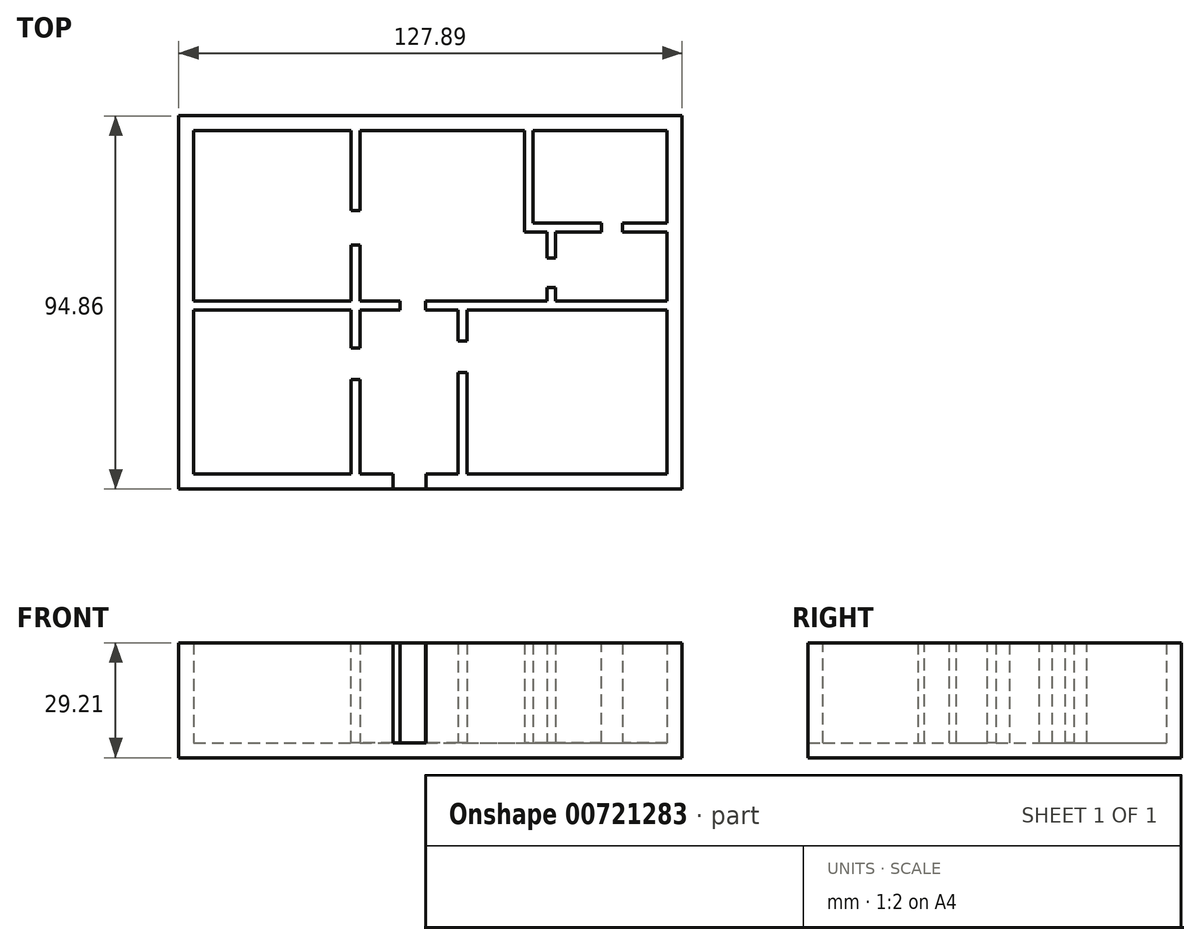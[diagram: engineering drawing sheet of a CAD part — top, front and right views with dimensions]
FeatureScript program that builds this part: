
annotation { "Feature Type Name" : "Feature", "Feature Type Description" : "" }
export const myFeature = defineFeature(function(context is Context, id is Id, definition is map)
    precondition{}
    {
        {
            var Q0;
            Q0=qCreatedBy(makeId("Top.planeOp"),FACE);
            var sketch = newSketch(context, id + "F0", { "sketchPlane" : qUnion([Q0])});
            skLineSegment(sketch, "E0.bottom", {"start": v(56.9, -47.76) * mm, "end": v(-70.99, -47.76) * mm});
            skLineSegment(sketch, "E0.top", {"start": v(56.9, 47.1) * mm, "end": v(-70.99, 47.1) * mm});
            skLineSegment(sketch, "E0.left", {"start": v(56.9, -47.76) * mm, "end": v(56.9, 47.1) * mm});
            skLineSegment(sketch, "E0.right", {"start": v(-70.99, -47.76) * mm, "end": v(-70.99, 47.1) * mm});
            skSolve(sketch);
        }
        {
            var Q0;
            Q0 = qSketchRegion(id + "F0", true);
            extrude(context, id + "F1", {"entities" : qUnion([Q0]), "depth" : 3.8 * mm, "offsetDistance" : 25.4 * mm});
        }
        {
            var Q0;
            Q0=makeQuery(id+"F1.opExtrude","CAP_FACE",FACE,{"disambiguationData":[OSD([sQuery(id+"F0.wireOp",EDGE,"E0.bottom"),sQuery(id+"F0.wireOp",EDGE,"E0.top"),sQuery(id+"F0.wireOp",EDGE,"E0.left"),sQuery(id+"F0.wireOp",EDGE,"E0.right")])],"isStart":false});
            var sketch = newSketch(context, id + "F2", { "sketchPlane" : qUnion([Q0])});
            skLineSegment(sketch, "E1.bottom", {"start": v(-70.99, -47.76) * mm, "end": v(56.9, -47.76) * mm});
            skLineSegment(sketch, "E1.top", {"start": v(-70.99, 47.1) * mm, "end": v(56.9, 47.1) * mm});
            skLineSegment(sketch, "E1.left", {"start": v(-70.99, -47.76) * mm, "end": v(-70.99, 47.1) * mm});
            skLineSegment(sketch, "E1.right", {"start": v(56.9, -47.76) * mm, "end": v(56.9, 47.1) * mm});
            skLineSegment(sketch, "E2.bottom", {"start": v(-67.18, -43.95) * mm, "end": v(53.09, -43.95) * mm});
            skLineSegment(sketch, "E2.top", {"start": v(-67.18, 43.3) * mm, "end": v(53.09, 43.3) * mm});
            skLineSegment(sketch, "E2.left", {"start": v(-67.18, -43.95) * mm, "end": v(-67.18, 43.3) * mm});
            skLineSegment(sketch, "E2.right", {"start": v(53.09, -43.95) * mm, "end": v(53.09, 43.3) * mm});
            skSolve(sketch);
        }
        {
            var Q0;
            Q0 = qSketchRegion(id + "F2", true);
            extrude(context, id + "F3", {"entities" : qUnion([Q0]), "operationType" : NewBodyOperationType.ADD, "depth" : 25.4 * mm, "offsetDistance" : 25.4 * mm});
        }
        {
            var Q0;
            Q0=makeQuery(id+"F1.opExtrude","CAP_FACE",FACE,{"disambiguationData":[OSD([sQuery(id+"F0.wireOp",EDGE,"E0.bottom"),sQuery(id+"F0.wireOp",EDGE,"E0.top"),sQuery(id+"F0.wireOp",EDGE,"E0.left"),sQuery(id+"F0.wireOp",EDGE,"E0.right")])],"isStart":false});
            var sketch = newSketch(context, id + "F4", { "sketchPlane" : qUnion([Q0])});
            skPoint(sketch, "E3.right.end.orphan", {"position": v(-27.18, 0) * mm});
            skLineSegment(sketch, "E4.bottom", {"start": v(-24.99, 0) * mm, "end": v(-24.98, 0) * mm});
            skLineSegment(sketch, "E4.top", {"start": v(-27.18, 43.3) * mm, "end": v(-24.98, 43.3) * mm});
            skLineSegment(sketch, "E4.left", {"start": v(-27.18, 0) * mm, "end": v(-27.18, 43.3) * mm});
            skLineSegment(sketch, "E4.right", {"start": v(-24.98, 0) * mm, "end": v(-24.98, 43.3) * mm});
            skPoint(sketch, "E5.firstSnap0", {"position": v(-67.18, -0.33) * mm});
            skLineSegment(sketch, "E5.bottom", {"start": v(-67.18, 0) * mm, "end": v(-27.18, 0) * mm});
            skLineSegment(sketch, "E5.top", {"start": v(-67.18, -2.2) * mm, "end": v(-24.99, -2.2) * mm});
            skLineSegment(sketch, "E5.left", {"start": v(-67.18, 0) * mm, "end": v(-67.18, -2.2) * mm});
            skLineSegment(sketch, "E5.right", {"start": v(-24.99, 0) * mm, "end": v(-24.99, -2.2) * mm});
            skSolve(sketch);
        }
        {
            var Q0;
            Q0 = qSketchRegion(id + "F4", true);
            extrude(context, id + "F5", {"entities" : qUnion([Q0]), "operationType" : NewBodyOperationType.ADD, "depth" : 25.4 * mm, "offsetDistance" : 25.4 * mm});
        }
        {
            var Q0;
            Q0=makeQuery(id+"F5.boolean.opBoolean","SPLIT",FACE,{"disambiguationData":[TD([makeQuery(id+"F3.opExtrude","SWEPT_FACE",FACE,{"disambiguationData":[OSD([sQuery(id+"F2.wireOp",EDGE,"E2.bottom")])]})])],"derivedFrom":makeQuery(id+"F1.opExtrude","CAP_FACE",FACE,{"disambiguationData":[OSD([sQuery(id+"F0.wireOp",EDGE,"E0.bottom"),sQuery(id+"F0.wireOp",EDGE,"E0.top"),sQuery(id+"F0.wireOp",EDGE,"E0.left"),sQuery(id+"F0.wireOp",EDGE,"E0.right")])],"isStart":false})});
            var sketch = newSketch(context, id + "F6", { "sketchPlane" : qUnion([Q0])});
            skLineSegment(sketch, "E6", {"start": v(-24.98, 0) * mm, "end": v(-24.99, -2.2) * mm});
            skPoint(sketch, "E7.start.orphan", {"position": v(0, -2.2) * mm});
            skLineSegment(sketch, "E8", {"start": v(0, 0) * mm, "end": v(0, -2.2) * mm});
            skLineSegment(sketch, "E9", {"start": v(0, -43.95) * mm, "end": v(-2.2, -43.95) * mm});
            skPoint(sketch, "E10.end.orphan", {"position": v(-2.2, -2.2) * mm});
            skLineSegment(sketch, "E11", {"start": v(-24.99, -2.2) * mm, "end": v(-24.99, -43.95) * mm});
            skLineSegment(sketch, "E12", {"start": v(-24.99, -43.95) * mm, "end": v(-27.2, -43.95) * mm});
            skLineSegment(sketch, "E13", {"start": v(-27.2, -43.95) * mm, "end": v(-27.2, -2.2) * mm});
            skLineSegment(sketch, "E14", {"start": v(-27.2, -2.2) * mm, "end": v(-24.99, -2.2) * mm});
            skLineSegment(sketch, "E15", {"start": v(-27.2, -43.95) * mm, "end": v(-24.99, -43.95) * mm});
            skLineSegment(sketch, "E16", {"start": v(-27.2, -43.95) * mm, "end": v(-67.18, -43.95) * mm});
            skSolve(sketch);
        }
        {
            var Q0;
            Q0 = qSketchRegion(id + "F6", true);
            extrude(context, id + "F7", {"entities" : qUnion([Q0]), "operationType" : NewBodyOperationType.ADD, "depth" : 25.4 * mm, "offsetDistance" : 25.4 * mm});
        }
        {
            var Q0;
            {var subQ2=makeQuery(id+"F3.opExtrude","SWEPT_FACE",FACE,{"disambiguationData":[OSD([sQuery(id+"F2.wireOp",EDGE,"E2.top")])]});var subQ3=makeQuery(id+"F3.opExtrude","SWEPT_FACE",FACE,{"disambiguationData":[OSD([sQuery(id+"F2.wireOp",EDGE,"E2.bottom")])]});Q0=makeQuery(id+"F7.boolean.opBoolean","SPLIT",FACE,{"disambiguationData":[TD([subQ2])],"derivedFrom":makeQuery(id+"F5.boolean.opBoolean","SPLIT",FACE,{"disambiguationData":[TD([subQ3])],"derivedFrom":makeQuery(id+"F1.opExtrude","CAP_FACE",FACE,{"disambiguationData":[OSD([sQuery(id+"F0.wireOp",EDGE,"E0.bottom"),sQuery(id+"F0.wireOp",EDGE,"E0.top"),sQuery(id+"F0.wireOp",EDGE,"E0.left"),sQuery(id+"F0.wireOp",EDGE,"E0.right")])],"isStart":false})})});}
            var sketch = newSketch(context, id + "F8", { "sketchPlane" : qUnion([Q0])});
            skLineSegment(sketch, "E17", {"start": v(0, -43.95) * mm, "end": v(0, 0) * mm});
            skLineSegment(sketch, "E18", {"start": v(0, 0) * mm, "end": v(53.09, 0) * mm});
            skLineSegment(sketch, "E19", {"start": v(53.09, 0) * mm, "end": v(53.09, -2.2) * mm});
            skLineSegment(sketch, "E20", {"start": v(53.09, -2.2) * mm, "end": v(2.2, -2.2) * mm});
            skLineSegment(sketch, "E21", {"start": v(2.2, -2.2) * mm, "end": v(2.2, -43.95) * mm});
            skLineSegment(sketch, "E22", {"start": v(2.2, -43.95) * mm, "end": v(0, -43.95) * mm});
            skPoint(sketch, "E23.orphan", {"position": v(0, -2.2) * mm});
            skSolve(sketch);
        }
        {
            var Q0;
            Q0 = qSketchRegion(id + "F8", true);
            extrude(context, id + "F9", {"entities" : qUnion([Q0]), "operationType" : NewBodyOperationType.ADD, "depth" : 25.4 * mm, "offsetDistance" : 25.4 * mm});
        }
        {
            var Q0;
            {var subQ2=makeQuery(id+"F3.opExtrude","SWEPT_FACE",FACE,{"disambiguationData":[OSD([sQuery(id+"F2.wireOp",EDGE,"E2.top")])]});var subQ3=makeQuery(id+"F3.opExtrude","SWEPT_FACE",FACE,{"disambiguationData":[OSD([sQuery(id+"F2.wireOp",EDGE,"E2.bottom")])]});Q0=makeQuery(id+"F9.boolean.opBoolean","SPLIT",FACE,{"disambiguationData":[TD([subQ2])],"derivedFrom":makeQuery(id+"F7.boolean.opBoolean","SPLIT",FACE,{"disambiguationData":[TD([subQ2])],"derivedFrom":makeQuery(id+"F5.boolean.opBoolean","SPLIT",FACE,{"disambiguationData":[TD([subQ3])],"derivedFrom":makeQuery(id+"F1.opExtrude","CAP_FACE",FACE,{"disambiguationData":[OSD([sQuery(id+"F0.wireOp",EDGE,"E0.bottom"),sQuery(id+"F0.wireOp",EDGE,"E0.top"),sQuery(id+"F0.wireOp",EDGE,"E0.left"),sQuery(id+"F0.wireOp",EDGE,"E0.right")])],"isStart":false})})})});}
            var sketch = newSketch(context, id + "F10", { "sketchPlane" : qUnion([Q0])});
            skLineSegment(sketch, "E24", {"start": v(-24.98, 0) * mm, "end": v(0, 0) * mm});
            skLineSegment(sketch, "E25", {"start": v(0, 0) * mm, "end": v(0, -2.2) * mm});
            skLineSegment(sketch, "E26", {"start": v(0, -2.2) * mm, "end": v(-24.99, -2.2) * mm});
            skLineSegment(sketch, "E27", {"start": v(-24.99, -2.2) * mm, "end": v(-26.96, -2.2) * mm});
            skLineSegment(sketch, "E28", {"start": v(-26.96, -2.2) * mm, "end": v(-26.96, 0) * mm});
            skLineSegment(sketch, "E29", {"start": v(-26.96, 0) * mm, "end": v(-24.98, 0) * mm});
            skSolve(sketch);
        }
        {
            var Q0;
            Q0 = qSketchRegion(id + "F10", true);
            extrude(context, id + "F11", {"entities" : qUnion([Q0]), "operationType" : NewBodyOperationType.ADD, "depth" : 25.4 * mm, "offsetDistance" : 25.4 * mm});
        }
        {
            var Q0;
            {var subQ1=makeQuery(id+"F3.opExtrude","SWEPT_FACE",FACE,{"disambiguationData":[OSD([sQuery(id+"F2.wireOp",EDGE,"E2.top")])]});var subQ5=makeQuery(id+"F3.opExtrude","SWEPT_FACE",FACE,{"disambiguationData":[OSD([sQuery(id+"F2.wireOp",EDGE,"E2.bottom")])]});Q0=makeQuery(id+"F11.boolean.opBoolean","SPLIT",FACE,{"disambiguationData":[TD([subQ1])],"derivedFrom":makeQuery(id+"F9.boolean.opBoolean","SPLIT",FACE,{"disambiguationData":[TD([subQ1])],"derivedFrom":makeQuery(id+"F7.boolean.opBoolean","SPLIT",FACE,{"disambiguationData":[TD([subQ1])],"derivedFrom":makeQuery(id+"F5.boolean.opBoolean","SPLIT",FACE,{"disambiguationData":[TD([subQ5])],"derivedFrom":makeQuery(id+"F1.opExtrude","CAP_FACE",FACE,{"disambiguationData":[OSD([sQuery(id+"F0.wireOp",EDGE,"E0.bottom"),sQuery(id+"F0.wireOp",EDGE,"E0.top"),sQuery(id+"F0.wireOp",EDGE,"E0.left"),sQuery(id+"F0.wireOp",EDGE,"E0.right")])],"isStart":false})})})})});}
            var sketch = newSketch(context, id + "F12", { "sketchPlane" : qUnion([Q0])});
            skLineSegment(sketch, "E30", {"start": v(22.56, 0) * mm, "end": v(22.56, 19.8) * mm});
            skLineSegment(sketch, "E31", {"start": v(22.56, 19.8) * mm, "end": v(53.09, 19.8) * mm});
            skLineSegment(sketch, "E32", {"start": v(53.09, 19.8) * mm, "end": v(53.09, 17.6) * mm});
            skLineSegment(sketch, "E33", {"start": v(53.09, 17.6) * mm, "end": v(22.56, 17.6) * mm});
            skLineSegment(sketch, "E34", {"start": v(22.56, 17.6) * mm, "end": v(24.77, 17.6) * mm});
            skLineSegment(sketch, "E35", {"start": v(24.77, 17.6) * mm, "end": v(24.77, 0) * mm});
            skLineSegment(sketch, "E36", {"start": v(24.77, 0) * mm, "end": v(22.56, 0) * mm});
            skSolve(sketch);
        }
        {
            var Q0;
            Q0 = qSketchRegion(id + "F12", true);
            extrude(context, id + "F13", {"entities" : qUnion([Q0]), "operationType" : NewBodyOperationType.ADD, "depth" : 25.4 * mm, "offsetDistance" : 25.4 * mm});
        }
        {
            var Q0;
            {var subQ1=makeQuery(id+"F3.opExtrude","SWEPT_FACE",FACE,{"disambiguationData":[OSD([sQuery(id+"F2.wireOp",EDGE,"E2.top")])]});var subQ6=makeQuery(id+"F3.opExtrude","SWEPT_FACE",FACE,{"disambiguationData":[OSD([sQuery(id+"F2.wireOp",EDGE,"E2.bottom")])]});Q0=makeQuery(id+"F13.boolean.opBoolean","SPLIT",FACE,{"disambiguationData":[TD([subQ1])],"derivedFrom":makeQuery(id+"F11.boolean.opBoolean","SPLIT",FACE,{"disambiguationData":[TD([subQ1])],"derivedFrom":makeQuery(id+"F9.boolean.opBoolean","SPLIT",FACE,{"disambiguationData":[TD([subQ1])],"derivedFrom":makeQuery(id+"F7.boolean.opBoolean","SPLIT",FACE,{"disambiguationData":[TD([subQ1])],"derivedFrom":makeQuery(id+"F5.boolean.opBoolean","SPLIT",FACE,{"disambiguationData":[TD([subQ6])],"derivedFrom":makeQuery(id+"F1.opExtrude","CAP_FACE",FACE,{"disambiguationData":[OSD([sQuery(id+"F0.wireOp",EDGE,"E0.bottom"),sQuery(id+"F0.wireOp",EDGE,"E0.top"),sQuery(id+"F0.wireOp",EDGE,"E0.left"),sQuery(id+"F0.wireOp",EDGE,"E0.right")])],"isStart":false})})})})})});}
            var sketch = newSketch(context, id + "F14", { "sketchPlane" : qUnion([Q0])});
            skLineSegment(sketch, "E37", {"start": v(53.09, 19.8) * mm, "end": v(53.09, 22.02) * mm});
            skPoint(sketch, "E38.orphan", {"position": v(19.05, 19.8) * mm});
            skPoint(sketch, "E39.start.orphan", {"position": v(16.84, 19.8) * mm});
            skLineSegment(sketch, "E40", {"start": v(53.09, 19.8) * mm, "end": v(16.84, 19.8) * mm});
            skLineSegment(sketch, "E41", {"start": v(53.09, 19.8) * mm, "end": v(53.09, 17.6) * mm});
            skLineSegment(sketch, "E42", {"start": v(53.09, 17.6) * mm, "end": v(16.84, 17.6) * mm});
            skLineSegment(sketch, "E43", {"start": v(16.84, 17.6) * mm, "end": v(16.84, 19.8) * mm});
            skLineSegment(sketch, "E44", {"start": v(16.84, 19.8) * mm, "end": v(16.84, 43.3) * mm});
            skLineSegment(sketch, "E45", {"start": v(16.84, 43.3) * mm, "end": v(19.05, 43.3) * mm});
            skLineSegment(sketch, "E46", {"start": v(19.05, 43.3) * mm, "end": v(19.05, 19.8) * mm});
            skSolve(sketch);
        }
        {
            var Q0;
            Q0 = qSketchRegion(id + "F14", true);
            extrude(context, id + "F15", {"entities" : qUnion([Q0]), "operationType" : NewBodyOperationType.ADD, "depth" : 25.4 * mm, "offsetDistance" : 25.4 * mm});
        }
        {
            var Q0;
            {var subQ0=sQuery(id+"F4.wireOp",EDGE,"E5.right");var subQ1=makeQuery(id+"F5.opExtrude","SWEPT_FACE",FACE,{"disambiguationData":[OSD([subQ0])]});var subQ3=sQuery(id+"F2.wireOp",EDGE,"E2.right");var subQ4=sQuery(id+"F2.wireOp",EDGE,"E2.bottom");Q0=makeQuery(id+"F9.boolean.opBoolean","SPLIT",FACE,{"disambiguationData":[TD([subQ1])],"derivedFrom":makeQuery(id+"F7.boolean.opBoolean","SPLIT",FACE,{"disambiguationData":[TD([makeQuery(id+"F3.opExtrude","SWEPT_FACE",FACE,{"disambiguationData":[OSD([subQ3])]})])],"derivedFrom":makeQuery(id+"F3.opExtrude","SWEPT_FACE",FACE,{"disambiguationData":[OSD([subQ4])]})})});}
            var sketch = newSketch(context, id + "F16", { "sketchPlane" : qUnion([Q0])});
            skLineSegment(sketch, "E47.bottom", {"start": v(8.18, 3.81) * mm, "end": v(16.54, 3.81) * mm});
            skLineSegment(sketch, "E47.left", {"start": v(8.18, 3.81) * mm, "end": v(8.18, 22.11) * mm});
            skLineSegment(sketch, "E47.right", {"start": v(16.54, 3.81) * mm, "end": v(16.54, 22.11) * mm});
            skLineSegment(sketch, "E48", {"start": v(16.54, 22.11) * mm, "end": v(16.54, 32) * mm});
            skLineSegment(sketch, "E49", {"start": v(8.18, 22.11) * mm, "end": v(8.18, 32) * mm});
            skLineSegment(sketch, "E50", {"start": v(16.54, 32) * mm, "end": v(8.18, 32) * mm});
            skSolve(sketch);
        }
        {
            var Q0;
            Q0 = qSketchRegion(id + "F16", true);
            extrude(context, id + "F17", {"entities" : qUnion([Q0]), "operationType" : NewBodyOperationType.REMOVE, "oppositeDirection" : true, "depth" : 25.4 * mm, "offsetDistance" : 25.4 * mm});
        }
        {
            var Q0;
            Q0=makeQuery(id+"F9.opExtrude","SWEPT_FACE",FACE,{"disambiguationData":[OSD([sQuery(id+"F8.wireOp",EDGE,"E17")])]});
            var sketch = newSketch(context, id + "F18", { "sketchPlane" : qUnion([Q0])});
            skLineSegment(sketch, "E51.bottom", {"start": v(10.1, 3.81) * mm, "end": v(18.16, 3.81) * mm});
            skLineSegment(sketch, "E51.left", {"start": v(10.1, 3.81) * mm, "end": v(10.1, 23.64) * mm});
            skLineSegment(sketch, "E51.right", {"start": v(18.16, 3.81) * mm, "end": v(18.16, 23.64) * mm});
            skLineSegment(sketch, "E52", {"start": v(18.16, 23.64) * mm, "end": v(18.16, 31.11) * mm});
            skLineSegment(sketch, "E53", {"start": v(10.1, 23.64) * mm, "end": v(10.1, 31.11) * mm});
            skLineSegment(sketch, "E54", {"start": v(10.1, 31.11) * mm, "end": v(18.16, 31.11) * mm});
            skSolve(sketch);
        }
        {
            var Q0;
            Q0 = qSketchRegion(id + "F18", true);
            extrude(context, id + "F19", {"entities" : qUnion([Q0]), "operationType" : NewBodyOperationType.REMOVE, "oppositeDirection" : true, "depth" : 25.4 * mm, "offsetDistance" : 25.4 * mm});
        }
        {
            var Q0;
            Q0=makeQuery(id+"F7.opExtrude","SWEPT_FACE",FACE,{"disambiguationData":[OSD([sQuery(id+"F6.wireOp",EDGE,"E13")])]});
            var sketch = newSketch(context, id + "F20", { "sketchPlane" : qUnion([Q0])});
            skLineSegment(sketch, "E55.bottom", {"start": v(11.88, 3.81) * mm, "end": v(19.86, 3.81) * mm});
            skLineSegment(sketch, "E55.left", {"start": v(11.88, 3.81) * mm, "end": v(11.88, 20.16) * mm});
            skLineSegment(sketch, "E55.right", {"start": v(19.86, 3.81) * mm, "end": v(19.86, 20.16) * mm});
            skLineSegment(sketch, "E56", {"start": v(11.88, 20.16) * mm, "end": v(11.88, 31.44) * mm});
            skLineSegment(sketch, "E57", {"start": v(19.86, 20.16) * mm, "end": v(19.86, 31.44) * mm});
            skLineSegment(sketch, "E58", {"start": v(19.86, 31.44) * mm, "end": v(11.88, 31.44) * mm});
            skSolve(sketch);
        }
        {
            var Q0;
            Q0 = qSketchRegion(id + "F20", true);
            extrude(context, id + "F21", {"entities" : qUnion([Q0]), "operationType" : NewBodyOperationType.REMOVE, "oppositeDirection" : true, "depth" : 9.65 * mm, "offsetDistance" : 25.4 * mm});
        }
        {
            var Q0;
            Q0=makeQuery(id+"F5.opExtrude","SWEPT_FACE",FACE,{"disambiguationData":[OSD([sQuery(id+"F4.wireOp",EDGE,"E4.left")])]});
            var sketch = newSketch(context, id + "F22", { "sketchPlane" : qUnion([Q0])});
            skLineSegment(sketch, "E59.bottom", {"start": v(-23.1, 3.81) * mm, "end": v(-14.3, 3.81) * mm});
            skLineSegment(sketch, "E59.left", {"start": v(-23.1, 3.81) * mm, "end": v(-23.1, 20) * mm});
            skLineSegment(sketch, "E59.right", {"start": v(-14.3, 3.81) * mm, "end": v(-14.3, 20) * mm});
            skLineSegment(sketch, "E60", {"start": v(-23.1, 20) * mm, "end": v(-23.1, 32.47) * mm});
            skLineSegment(sketch, "E61", {"start": v(-14.3, 20) * mm, "end": v(-14.3, 32.47) * mm});
            skLineSegment(sketch, "E62", {"start": v(-14.3, 32.47) * mm, "end": v(-23.1, 32.47) * mm});
            skSolve(sketch);
        }
        {
            var Q0;
            Q0 = qSketchRegion(id + "F22", true);
            extrude(context, id + "F23", {"entities" : qUnion([Q0]), "operationType" : NewBodyOperationType.REMOVE, "oppositeDirection" : true, "depth" : 6.38 * mm, "offsetDistance" : 25.4 * mm});
        }
        {
            var Q0;
            Q0=makeQuery(id+"F13.opExtrude","SWEPT_FACE",FACE,{"disambiguationData":[OSD([sQuery(id+"F12.wireOp",EDGE,"E30")])]});
            var sketch = newSketch(context, id + "F24", { "sketchPlane" : qUnion([Q0])});
            skLineSegment(sketch, "E63.bottom", {"start": v(-10.95, 3.81) * mm, "end": v(-3.42, 3.81) * mm});
            skLineSegment(sketch, "E63.left", {"start": v(-10.95, 3.81) * mm, "end": v(-10.95, 22.26) * mm});
            skLineSegment(sketch, "E63.right", {"start": v(-3.42, 3.81) * mm, "end": v(-3.42, 22.26) * mm});
            skLineSegment(sketch, "E64", {"start": v(-10.95, 22.26) * mm, "end": v(-10.95, 32.58) * mm});
            skLineSegment(sketch, "E65", {"start": v(-10.95, 32.58) * mm, "end": v(-3.42, 32.58) * mm});
            skLineSegment(sketch, "E66", {"start": v(-3.42, 32.58) * mm, "end": v(-3.42, 22.26) * mm});
            skSolve(sketch);
        }
        {
            var Q0;
            Q0 = qSketchRegion(id + "F24", true);
            extrude(context, id + "F25", {"entities" : qUnion([Q0]), "operationType" : NewBodyOperationType.REMOVE, "oppositeDirection" : true, "depth" : 11.43 * mm, "offsetDistance" : 25.4 * mm});
        }
        {
            var Q0;
            Q0=makeQuery(id+"F13.opExtrude","SWEPT_FACE",FACE,{"disambiguationData":[OSD([sQuery(id+"F12.wireOp",EDGE,"E33")])]});
            var sketch = newSketch(context, id + "F26", { "sketchPlane" : qUnion([Q0])});
            skLineSegment(sketch, "E67.bottom", {"start": v(36.45, 3.81) * mm, "end": v(41.72, 3.81) * mm});
            skLineSegment(sketch, "E67.left", {"start": v(36.45, 3.81) * mm, "end": v(36.45, 21.93) * mm});
            skLineSegment(sketch, "E67.right", {"start": v(41.72, 3.81) * mm, "end": v(41.72, 21.93) * mm});
            skLineSegment(sketch, "E68", {"start": v(36.45, 21.93) * mm, "end": v(36.45, 34.72) * mm});
            skLineSegment(sketch, "E69", {"start": v(36.45, 34.72) * mm, "end": v(41.72, 34.72) * mm});
            skLineSegment(sketch, "E70", {"start": v(41.72, 34.72) * mm, "end": v(41.72, 21.24) * mm});
            skSolve(sketch);
        }
        {
            var Q0;
            Q0 = qSketchRegion(id + "F26", true);
            extrude(context, id + "F27", {"entities" : qUnion([Q0]), "operationType" : NewBodyOperationType.REMOVE, "oppositeDirection" : true, "depth" : 11.43 * mm, "offsetDistance" : 25.4 * mm});
        }
        {
            var Q0;
            Q0=makeQuery(id+"F11.opExtrude","SWEPT_FACE",FACE,{"disambiguationData":[OSD([sQuery(id+"F10.wireOp",EDGE,"E26"),sQuery(id+"F10.wireOp",EDGE,"E27")])]});
            var sketch = newSketch(context, id + "F28", { "sketchPlane" : qUnion([Q0])});
            skLineSegment(sketch, "E71.bottom", {"start": v(-14.76, 3.81) * mm, "end": v(-8.26, 3.81) * mm});
            skLineSegment(sketch, "E71.left", {"start": v(-14.76, 3.81) * mm, "end": v(-14.76, 18.13) * mm});
            skLineSegment(sketch, "E71.right", {"start": v(-8.26, 3.81) * mm, "end": v(-8.26, 18.13) * mm});
            skLineSegment(sketch, "E72", {"start": v(-14.76, 18.13) * mm, "end": v(-14.76, 34.86) * mm});
            skLineSegment(sketch, "E73", {"start": v(-14.76, 34.86) * mm, "end": v(-8.26, 34.86) * mm});
            skLineSegment(sketch, "E74", {"start": v(-8.26, 34.86) * mm, "end": v(-8.26, 18.13) * mm});
            skSolve(sketch);
        }
        {
            var Q0;
            Q0 = qSketchRegion(id + "F28", true);
            extrude(context, id + "F29", {"entities" : qUnion([Q0]), "operationType" : NewBodyOperationType.REMOVE, "oppositeDirection" : true, "depth" : 10.4 * mm, "offsetDistance" : 25.4 * mm});
        }
    });
